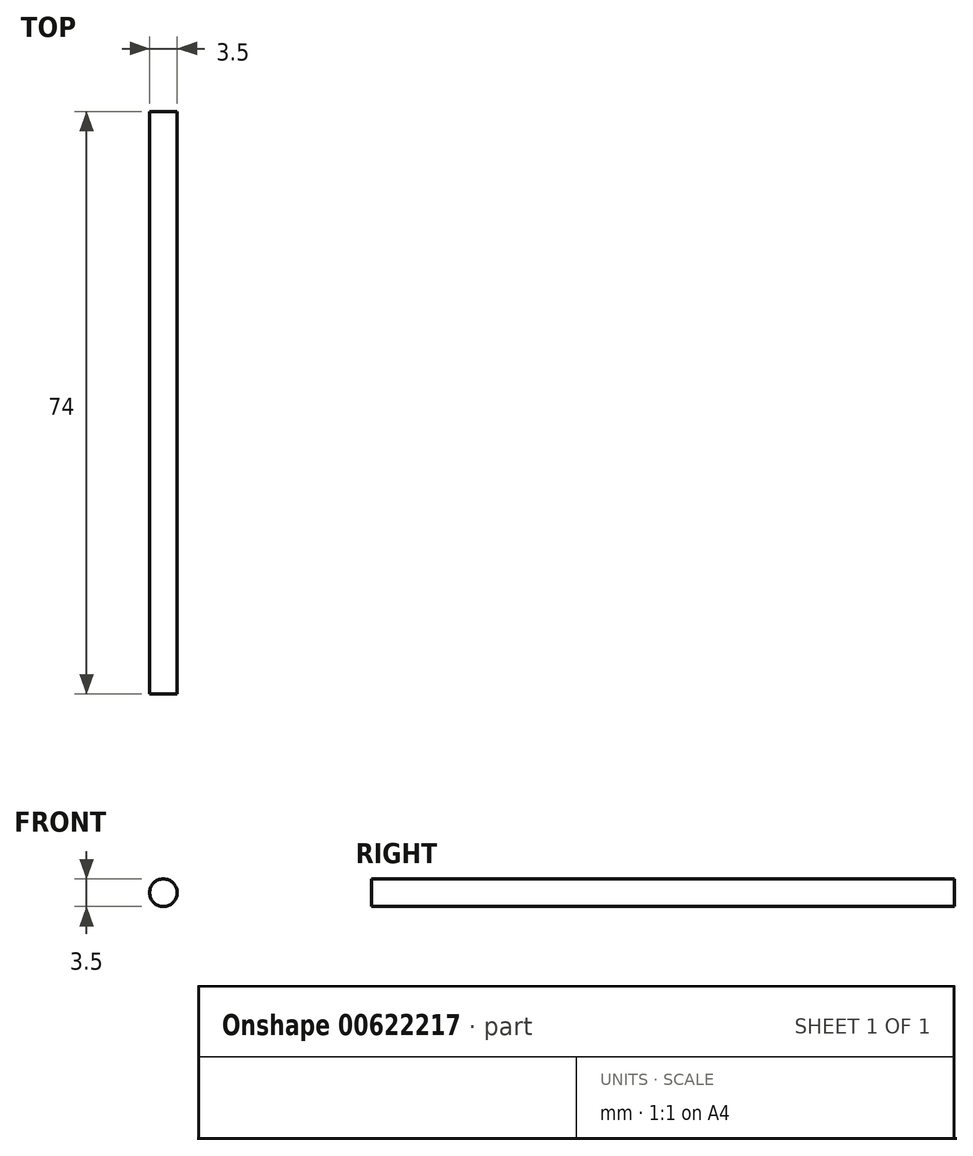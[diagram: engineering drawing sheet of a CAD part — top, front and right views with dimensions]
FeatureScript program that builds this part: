
annotation { "Feature Type Name" : "Feature", "Feature Type Description" : "" }
export const myFeature = defineFeature(function(context is Context, id is Id, definition is map)
    precondition{}
    {
        {
            var Q0;
            Q0=qCreatedBy(makeId("Front.planeOp"),FACE);
            var sketch = newSketch(context, id + "F0", { "sketchPlane" : qUnion([Q0])});
            skCircle(sketch, "E0", {"center": v(0, 0) * mm, "radius": 1.75 * mm});
            skSolve(sketch);
        }
        {
            var Q0;
            Q0=qSketchRegion(id+"F0",true);
            extrude(context, id + "F1", {"entities" : qUnion([Q0]), "depth" : 74 * mm, "offsetDistance" : 25 * mm});
        }
    });
